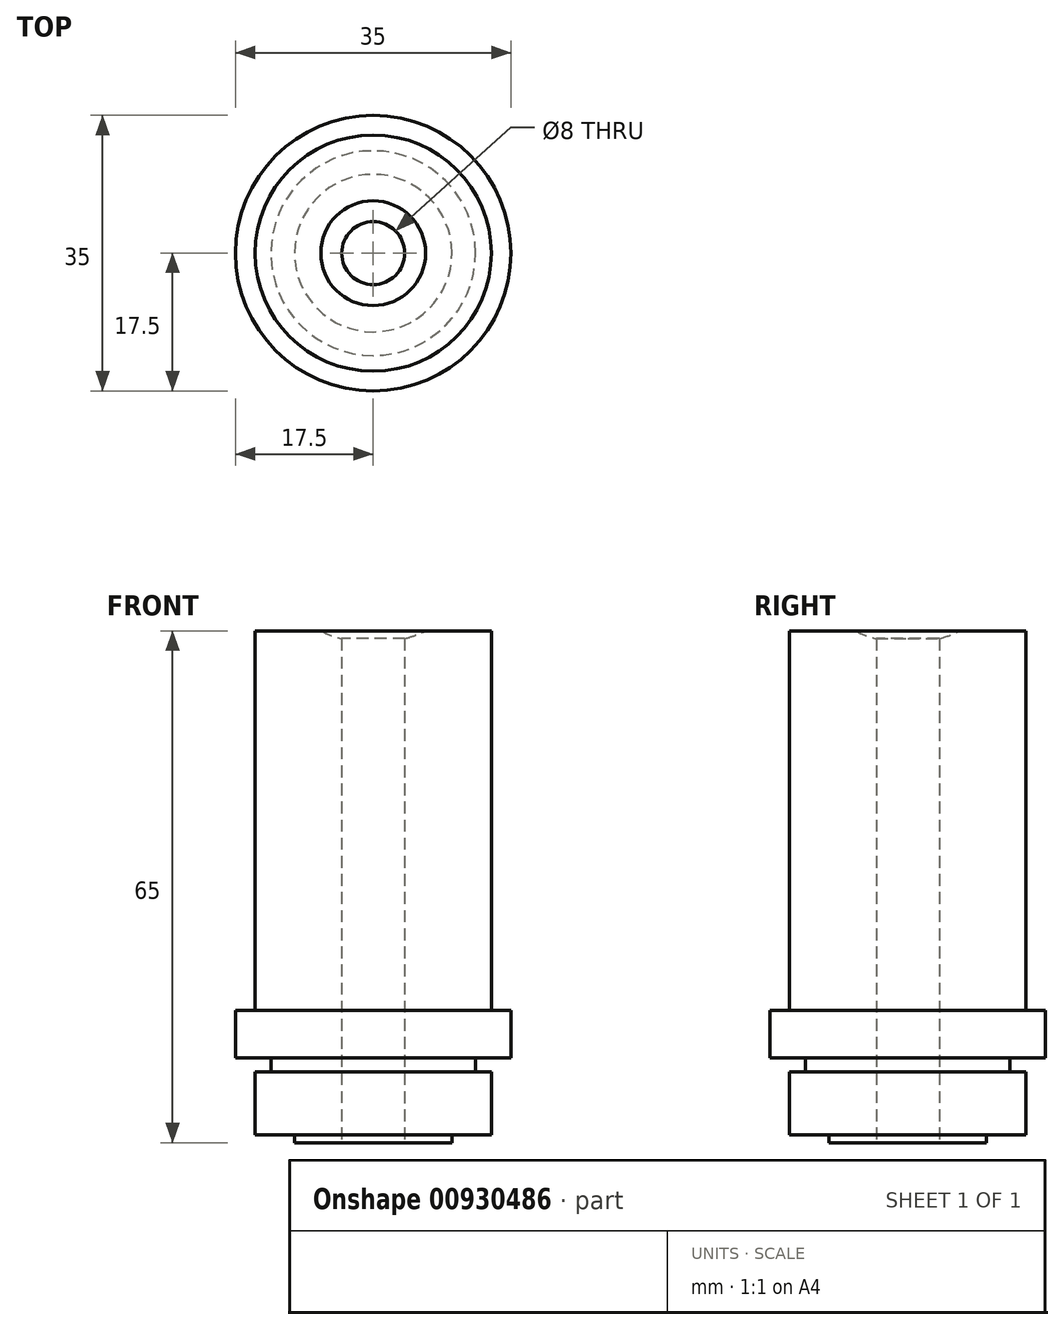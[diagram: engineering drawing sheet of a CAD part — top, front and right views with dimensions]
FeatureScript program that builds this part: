
annotation { "Feature Type Name" : "Feature", "Feature Type Description" : "" }
export const myFeature = defineFeature(function(context is Context, id is Id, definition is map)
    precondition{}
    {
        {
            var Q0;
            Q0=qCreatedBy(makeId("Right.planeOp"),FACE);
            var sketch = newSketch(context, id + "F0", { "sketchPlane" : qUnion([Q0])});
            skLineSegment(sketch, "E0", {"start": v(0, 0) * mm, "end": v(-10, 0) * mm});
            skLineSegment(sketch, "E1", {"start": v(-10, 0) * mm, "end": v(-10, 1) * mm});
            skLineSegment(sketch, "E2", {"start": v(-10, 1) * mm, "end": v(-15, 1) * mm});
            skLineSegment(sketch, "E3", {"start": v(-15, 1) * mm, "end": v(-15, 9) * mm});
            skLineSegment(sketch, "E4", {"start": v(-15, 9) * mm, "end": v(-13, 9) * mm});
            skLineSegment(sketch, "E5", {"start": v(-13, 9) * mm, "end": v(-13, 10.8) * mm});
            skLineSegment(sketch, "E6", {"start": v(-13, 10.8) * mm, "end": v(-17.5, 10.8) * mm});
            skPoint(sketch, "E7.orphan", {"position": v(0, 10.8) * mm});
            skLineSegment(sketch, "E8", {"start": v(-17.5, 10.8) * mm, "end": v(-17.5, 16.8) * mm});
            skLineSegment(sketch, "E9", {"start": v(-17.5, 16.8) * mm, "end": v(-15, 16.8) * mm});
            skLineSegment(sketch, "E10", {"start": v(-15, 16.8) * mm, "end": v(-15, 65) * mm});
            skLineSegment(sketch, "E11", {"start": v(-15, 65) * mm, "end": v(-6.65, 65) * mm});
            skArc(sketch, "E12", {"start": v(-6.65, 65) * mm, "mid": v(-3.4, 63.88) * mm, "end": v(0, 63.5) * mm});
            skPoint(sketch, "E13.orphan", {"position": v(0, 65) * mm});
            skLineSegment(sketch, "E14.MirrorCS", {"start": v(17.5, 16.8) * mm, "end": v(15, 16.8) * mm});
            skLineSegment(sketch, "E15.MirrorCS", {"start": v(13, 10.8) * mm, "end": v(17.5, 10.8) * mm});
            skLineSegment(sketch, "E16.MirrorCS", {"start": v(10, 1) * mm, "end": v(15, 1) * mm});
            skLineSegment(sketch, "E17.MirrorCS", {"start": v(10, 0) * mm, "end": v(10, 1) * mm});
            skLineSegment(sketch, "E18.MirrorCS", {"start": v(15, 9) * mm, "end": v(13, 9) * mm});
            skLineSegment(sketch, "E19.MirrorCS", {"start": v(13, 9) * mm, "end": v(13, 10.8) * mm});
            skLineSegment(sketch, "E20.MirrorCS", {"start": v(15, 16.8) * mm, "end": v(15, 65) * mm});
            skLineSegment(sketch, "E21.MirrorCS", {"start": v(15, 65) * mm, "end": v(6.65, 65) * mm});
            skLineSegment(sketch, "E22.MirrorCS", {"start": v(17.5, 10.8) * mm, "end": v(17.5, 16.8) * mm});
            skLineSegment(sketch, "E23.MirrorCS", {"start": v(0, 0) * mm, "end": v(10, 0) * mm});
            skLineSegment(sketch, "E24.MirrorCS", {"start": v(15, 1) * mm, "end": v(15, 9) * mm});
            skArc(sketch, "E25.MirrorCS", {"start": v(6.65, 65) * mm, "mid": v(3.4, 63.88) * mm, "end": v(0, 63.5) * mm});
            skLineSegment(sketch, "E26", {"start": v(0, 79) * mm, "end": v(0, -34.24) * mm});
            skSolve(sketch);
        }
        {
            var Q0;
            {var subQ0=sQuery(id+"F0.wireOp",EDGE,"E0");Q0=makeQuery(id+"F0.imprint","IMPRINT",FACE,{"disambiguationData":[TD([[makeQuery(id+"F0.imprint","IMPRINT",EDGE,{"derivedFrom":subQ0}),-1.0]])]});}
            var Q1;
            Q1=sQuery(id+"F0.wireOp",EDGE,"E26");
            revolve(context, id + "F1", {"surfaceOperationType" : NewSurfaceOperationType.NEW, "entities" : qUnion([Q0]), "axis" : qUnion([Q1]), "revolveType" : RevolveType.FULL});
        }
        {
            var Q0;
            Q0=qCreatedBy(makeId("Top.planeOp"),FACE);
            var sketch = newSketch(context, id + "F2", { "sketchPlane" : qUnion([Q0])});
            skCircle(sketch, "E27", {"center": v(0, 0) * mm, "radius": 4 * mm});
            skSolve(sketch);
        }
        {
            var Q0;
            Q0=makeQuery(id+"F2.imprint","IMPRINT",FACE,{"disambiguationData":[TD([[makeQuery(id+"F2.imprint","IMPRINT",EDGE,{"derivedFrom":sQuery(id+"F2.wireOp",EDGE,"E27")}),1.0]])]});
            extrude(context, id + "F3", {"entities" : qUnion([Q0]), "operationType" : NewBodyOperationType.REMOVE, "depth" : 70 * mm, "offsetDistance" : 25 * mm});
        }
    });
